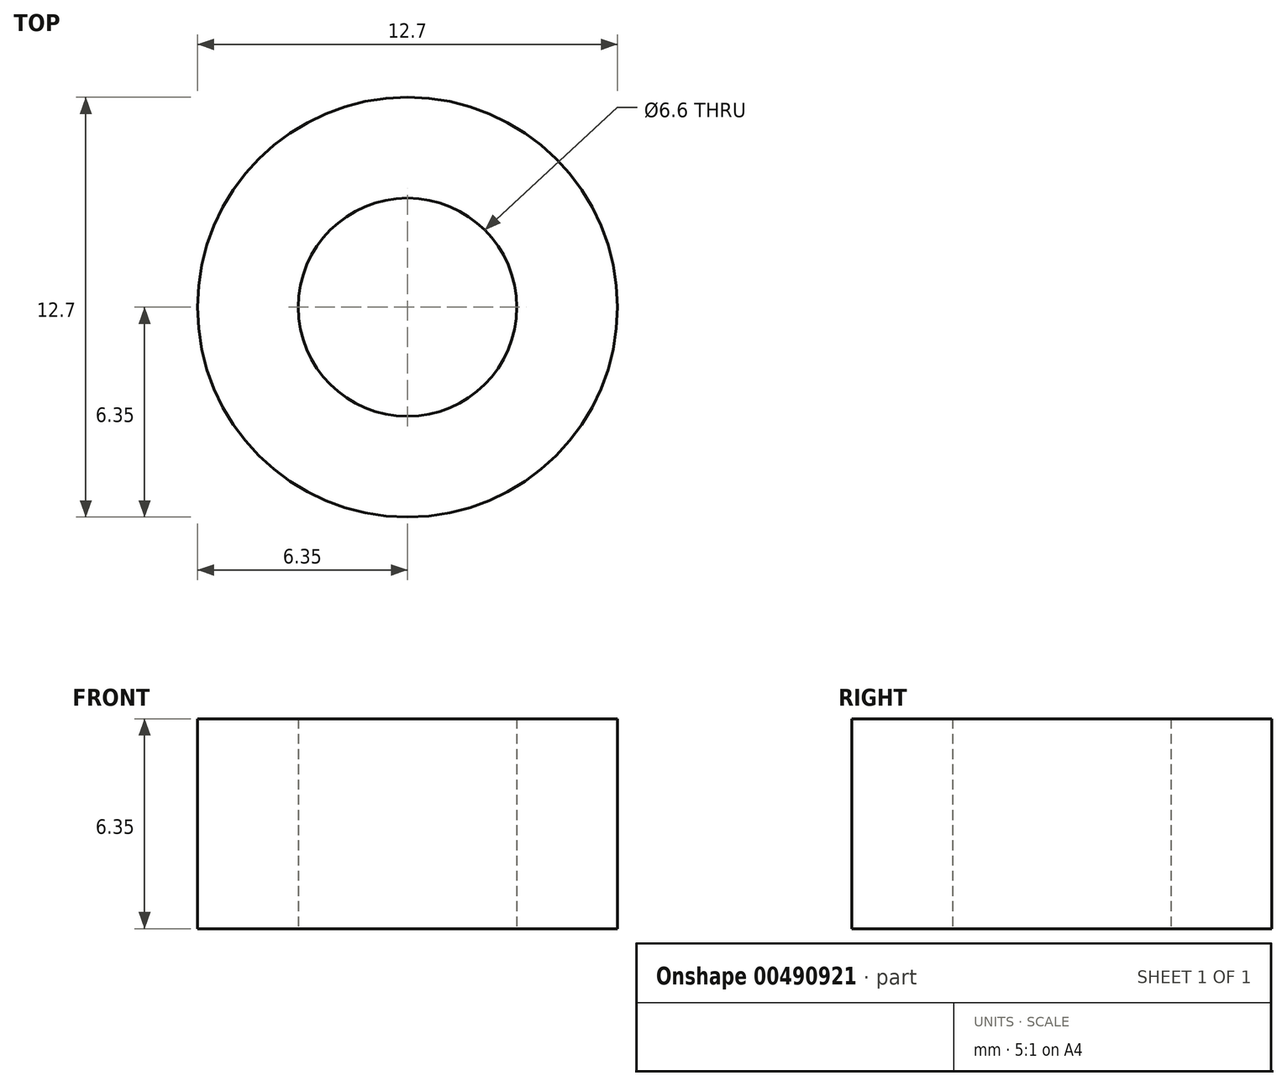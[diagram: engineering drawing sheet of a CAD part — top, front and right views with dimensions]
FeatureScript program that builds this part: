
annotation { "Feature Type Name" : "Feature", "Feature Type Description" : "" }
export const myFeature = defineFeature(function(context is Context, id is Id, definition is map)
    precondition{}
    {
        {
            var Q0;
            Q0=qCreatedBy(makeId("Top.planeOp"),FACE);
            var sketch = newSketch(context, id + "F0", { "sketchPlane" : qUnion([Q0])});
            skCircle(sketch, "E0", {"center": v(0, 0) * mm, "radius": 6.35 * mm});
            skCircle(sketch, "E1", {"center": v(0, 0) * mm, "radius": 3.3 * mm});
            skSolve(sketch);
        }
        {
            var Q0;
            Q0 = qSketchRegion(id + "F0", true);
            extrude(context, id + "F1", {"entities" : qUnion([Q0]), "depth" : 6.35 * mm});
        }
    });
